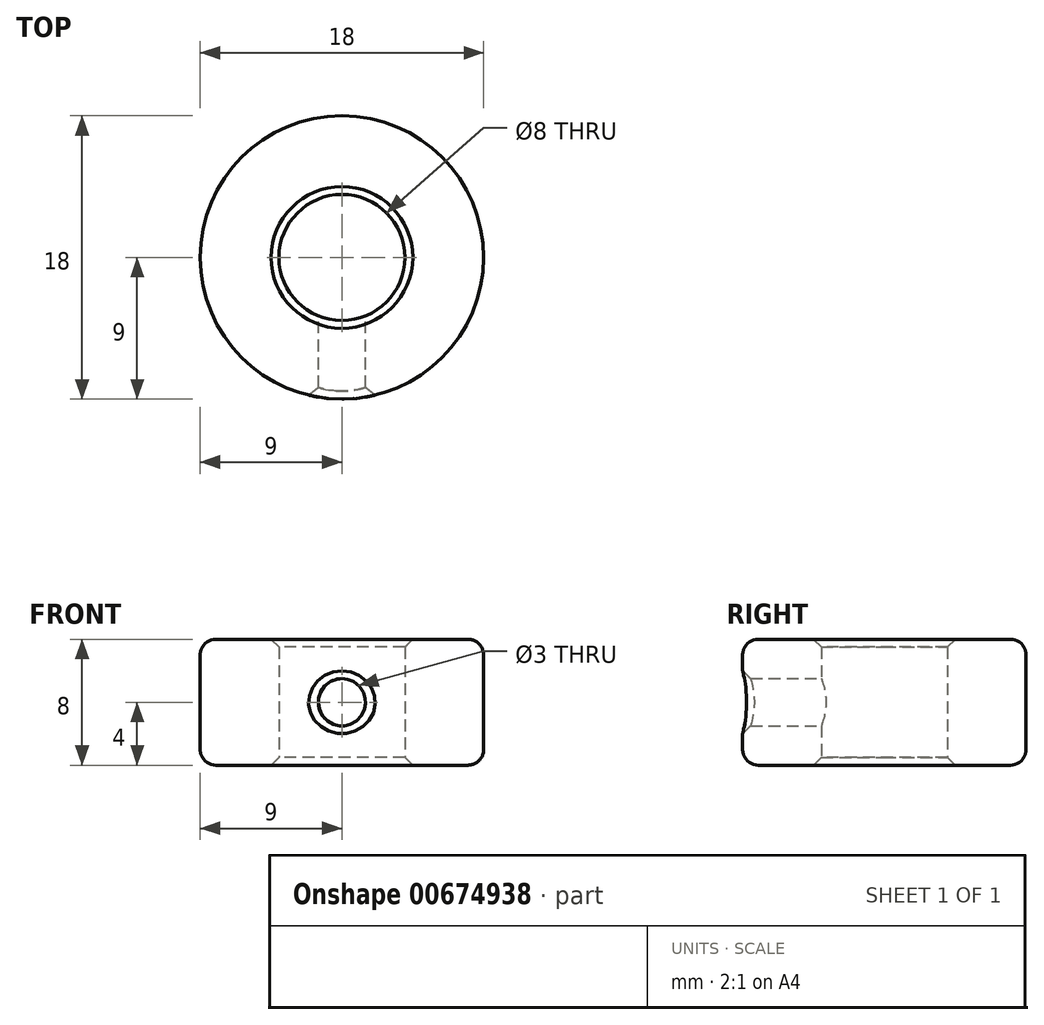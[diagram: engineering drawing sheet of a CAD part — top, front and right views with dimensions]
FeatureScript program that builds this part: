
annotation { "Feature Type Name" : "Feature", "Feature Type Description" : "" }
export const myFeature = defineFeature(function(context is Context, id is Id, definition is map)
    precondition{}
    {
        {
            var Q0;
            Q0=qCreatedBy(makeId("Top.planeOp"),FACE);
            var sketch = newSketch(context, id + "F0", { "sketchPlane" : qUnion([Q0])});
            skCircle(sketch, "E0", {"center": v(0, 0) * mm, "radius": 9 * mm});
            skCircle(sketch, "E1", {"center": v(0, 0) * mm, "radius": 4 * mm});
            skSolve(sketch);
        }
        {
            var Q0;
            Q0=makeQuery(id+"F0.imprint","IMPRINT",FACE,{"disambiguationData":[TD([[makeQuery(id+"F0.imprint","IMPRINT",EDGE,{"derivedFrom":sQuery(id+"F0.wireOp",EDGE,"E0")}),1.0]])]});
            extrude(context, id + "F1", {"entities" : qUnion([Q0]), "depth" : 8 * mm, "offsetDistance" : 25 * mm});
        }
        {
            var Q0;
            Q0=makeQuery(id+"F1.opExtrude","CAP_EDGE",EDGE,{"disambiguationData":[OSD([sQuery(id+"F0.wireOp",EDGE,"E0")])],"isStart":false});
            var Q1;
            Q1=makeQuery(id+"F1.opExtrude","CAP_EDGE",EDGE,{"disambiguationData":[OSD([sQuery(id+"F0.wireOp",EDGE,"E0")])],"isStart":true});
            fillet(context, id + "F2", {"entities" : qUnion([Q0, Q1]), "radius" : 1 * mm, "tangentPropagation" : true, "allowEdgeOverflow" : false});
        }
        {
            var Q0;
            Q0=qCreatedBy(makeId("Front.planeOp"),FACE);
            var sketch = newSketch(context, id + "F3", { "sketchPlane" : qUnion([Q0])});
            skLineSegment(sketch, "E2", {"start": v(0, 0) * mm, "end": v(0, 4) * mm});
            skCircle(sketch, "E3", {"center": v(0, 4) * mm, "radius": 1.5 * mm});
            skSolve(sketch);
        }
        {
            var Q0;
            Q0=makeQuery(id+"F3.imprint","IMPRINT",FACE,{"disambiguationData":[TD([[makeQuery(id+"F3.imprint","IMPRINT",EDGE,{"derivedFrom":sQuery(id+"F3.wireOp",EDGE,"E3")}),1.0]])]});
            extrude(context, id + "F4", {"entities" : qUnion([Q0]), "operationType" : NewBodyOperationType.REMOVE, "depth" : 25 * mm, "offsetDistance" : 25 * mm});
        }
        {
            var Q0;
            Q0=makeQuery(id+"F1.opExtrude","CAP_EDGE",EDGE,{"disambiguationData":[OSD([sQuery(id+"F0.wireOp",EDGE,"E1")])],"isStart":false});
            var Q1;
            Q1=makeQuery(id+"F1.opExtrude","CAP_EDGE",EDGE,{"disambiguationData":[OSD([sQuery(id+"F0.wireOp",EDGE,"E1")])],"isStart":true});
            var Q2;
            Q2=makeQuery(id+"F4.boolean.opBoolean","INTERSECT",EDGE,{"derivedFrom":[makeQuery(id+"F1.opExtrude","SWEPT_FACE",FACE,{"disambiguationData":[OSD([sQuery(id+"F0.wireOp",EDGE,"E0")])]}),makeQuery(id+"F4.opExtrude","SWEPT_FACE",FACE,{"disambiguationData":[OSD([sQuery(id+"F3.wireOp",EDGE,"E3")])]})]});
            chamfer(context, id + "F5", {"entities" : qUnion([Q0, Q1, Q2]), "width" : 0.5 * mm, "tangentPropagation" : true});
        }
    });
